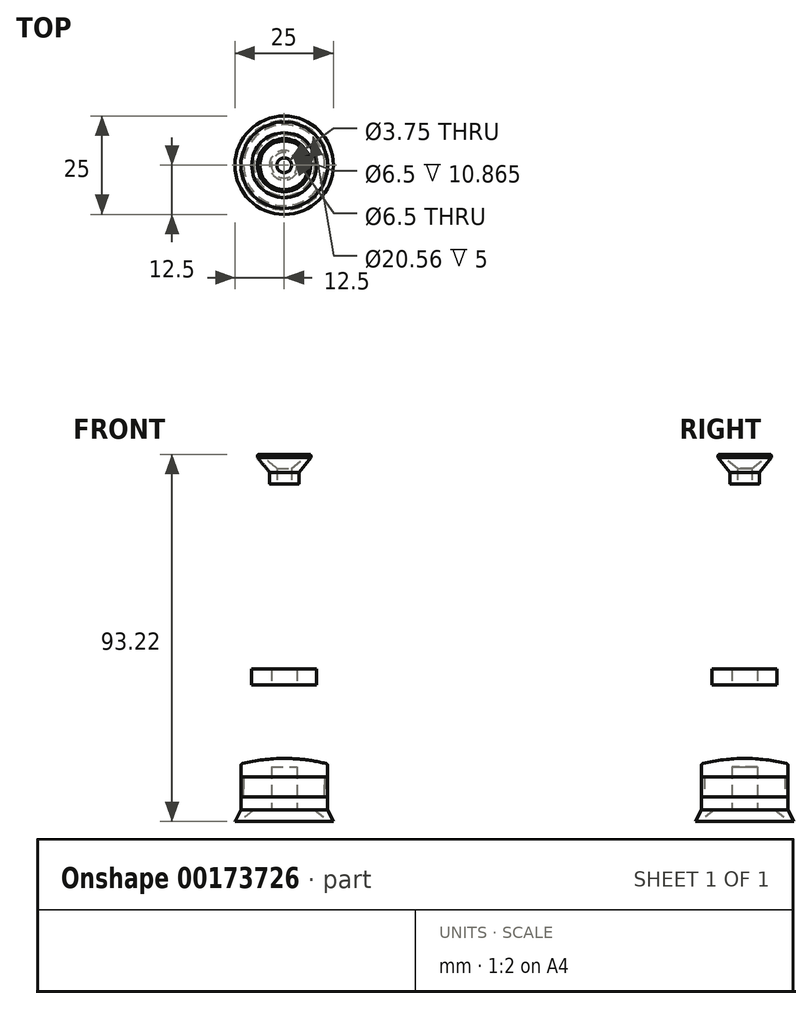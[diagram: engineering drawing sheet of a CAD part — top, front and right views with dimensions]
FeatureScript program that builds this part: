
annotation { "Feature Type Name" : "Feature", "Feature Type Description" : "" }
export const myFeature = defineFeature(function(context is Context, id is Id, definition is map)
    precondition{}
    {
        {
            var Q0;
            Q0=qCreatedBy(makeId("Front.planeOp"),FACE);
            var sketch = newSketch(context, id + "F0", { "sketchPlane" : qUnion([Q0])});
            skLineSegment(sketch, "E0.bottom", {"start": v(0, 0) * mm, "end": v(9, 0) * mm});
            skLineSegment(sketch, "E0.top", {"start": v(0, 18) * mm, "end": v(9, 18) * mm});
            skLineSegment(sketch, "E0.left", {"start": v(0, 0) * mm, "end": v(0, 18) * mm});
            skLineSegment(sketch, "E0.right", {"start": v(9, 0) * mm, "end": v(9, 18) * mm});
            skArc(sketch, "E1", {"start": v(9, 14.86) * mm, "mid": v(4.77, 17.2) * mm, "end": v(0, 18) * mm});
            skLineSegment(sketch, "E2.bottom", {"start": v(0, 0) * mm, "end": v(3.25, 0) * mm});
            skLineSegment(sketch, "E2.top", {"start": v(0, 15) * mm, "end": v(3.25, 15) * mm});
            skLineSegment(sketch, "E2.left", {"start": v(0, 0) * mm, "end": v(0, 15) * mm});
            skLineSegment(sketch, "E2.right", {"start": v(3.25, 0) * mm, "end": v(3.25, 15) * mm});
            skLineSegment(sketch, "E3.bottom", {"start": v(3.25, 0) * mm, "end": v(8.25, 0) * mm});
            skLineSegment(sketch, "E3.top", {"start": v(3.25, 4) * mm, "end": v(8.25, 4) * mm});
            skLineSegment(sketch, "E3.left", {"start": v(3.25, 0) * mm, "end": v(3.25, 4) * mm});
            skLineSegment(sketch, "E3.right", {"start": v(8.25, 0) * mm, "end": v(8.25, 4) * mm});
            skSolve(sketch);
        }
        {
            var Q0;
            {var subQ2=sQuery(id+"F0.wireOp",EDGE,"E0.bottom");Q0=makeQuery(id+"F0.imprint","IMPRINT",FACE,{"disambiguationData":[TD([[makeQuery(id+"F0.imprint","IMPRINT",EDGE,{"derivedFrom":subQ2}),1.0]])]});}
            var Q1;
            Q1=sQuery(id+"F0.wireOp",EDGE,"E0.left");
            revolve(context, id + "F1", {"entities" : qUnion([Q0]), "axis" : qUnion([Q1]), "revolveType" : RevolveType.FULL});
        }
        {
            var Q0;
            Q0=qCreatedBy(makeId("Front.planeOp"),FACE);
            var sketch = newSketch(context, id + "F2", { "sketchPlane" : qUnion([Q0])});
            skLineSegment(sketch, "E4.bottom", {"start": v(0, 50) * mm, "end": v(6.75, 50) * mm});
            skLineSegment(sketch, "E4.top", {"start": v(0, 58.5) * mm, "end": v(6.75, 58.5) * mm});
            skLineSegment(sketch, "E4.left", {"start": v(0, 50) * mm, "end": v(0, 58.5) * mm});
            skLineSegment(sketch, "E4.right", {"start": v(6.75, 50) * mm, "end": v(6.75, 58.5) * mm});
            skLineSegment(sketch, "E5.bottom", {"start": v(0, 50) * mm, "end": v(5.5, 50) * mm});
            skLineSegment(sketch, "E5.top", {"start": v(0, 51) * mm, "end": v(5.5, 51) * mm});
            skLineSegment(sketch, "E5.left", {"start": v(0, 50) * mm, "end": v(0, 51) * mm});
            skLineSegment(sketch, "E5.right", {"start": v(5.5, 50) * mm, "end": v(5.5, 51) * mm});
            skLineSegment(sketch, "E6.bottom", {"start": v(0, 51) * mm, "end": v(3.75, 51) * mm});
            skLineSegment(sketch, "E6.top", {"start": v(0, 54) * mm, "end": v(3.75, 54) * mm});
            skLineSegment(sketch, "E6.left", {"start": v(0, 51) * mm, "end": v(0, 54) * mm});
            skLineSegment(sketch, "E6.right", {"start": v(3.75, 51) * mm, "end": v(3.75, 54) * mm});
            skLineSegment(sketch, "E7", {"start": v(3.75, 54) * mm, "end": v(6.75, 57.75) * mm});
            skPoint(sketch, "E8.oppositeSnap0", {"position": v(1.87, 54) * mm});
            skLineSegment(sketch, "E8.bottom", {"start": v(0, 50) * mm, "end": v(1.87, 50) * mm});
            skLineSegment(sketch, "E8.top", {"start": v(0, 58.5) * mm, "end": v(1.87, 58.5) * mm});
            skLineSegment(sketch, "E8.right", {"start": v(1.87, 50) * mm, "end": v(1.87, 58.5) * mm});
            skLineSegment(sketch, "E9", {"start": v(1.87, 55) * mm, "end": v(6.2, 58.5) * mm});
            skArc(sketch, "E10", {"start": v(6.75, 58.05) * mm, "mid": v(6.73, 58.3) * mm, "end": v(6.6, 58.5) * mm});
            skSolve(sketch);
        }
        {
            var Q0;
            {var subQ0=sQuery(id+"F2.wireOp",EDGE,"E7");Q0=makeQuery(id+"F2.imprint","IMPRINT",FACE,{"disambiguationData":[TD([[makeQuery(id+"F2.imprint","IMPRINT",EDGE,{"derivedFrom":subQ0}),1.0]])]});}
            var Q1;
            {var subQ0=sQuery(id+"F2.wireOp",EDGE,"E6.right");Q1=makeQuery(id+"F2.imprint","IMPRINT",FACE,{"disambiguationData":[TD([[makeQuery(id+"F2.imprint","IMPRINT",EDGE,{"derivedFrom":subQ0}),1.0]])]});}
            var Q2;
            {var subQ4=sQuery(id+"F2.wireOp",EDGE,"E5.bottom");Q2=makeQuery(id+"F2.imprint","IMPRINT",FACE,{"disambiguationData":[TD([[makeQuery(id+"F2.imprint","IMPRINT",EDGE,{"derivedFrom":subQ4}),1.0]])]});}
            var Q3;
            Q3=sQuery(id+"F2.wireOp",EDGE,"E4.left");
            revolve(context, id + "F3", {"entities" : qUnion([Q0, Q1, Q2]), "axis" : qUnion([Q3]), "revolveType" : RevolveType.FULL});
        }
        {
            var Q0;
            Q0=makeQuery(id+"F3.opRevolve","SWEPT_EDGE",EDGE,{"disambiguationData":[OSD([sQuery(id+"F2.wireOp",EDGE,"E5.top"),sQuery(id+"F2.wireOp",EDGE,"E5.right")])]});
            fillet(context, id + "F4", {"entities" : qUnion([Q0]), "radius" : .2 * mm, "tangentPropagation" : true, "allowEdgeOverflow" : false});
        }
        {
            var Q0;
            Q0=qCreatedBy(makeId("Front.planeOp"),FACE);
            var sketch = newSketch(context, id + "F5", { "sketchPlane" : qUnion([Q0])});
            skLineSegment(sketch, "E11.bottom", {"start": v(0, -34.72) * mm, "end": v(12.5, -34.72) * mm});
            skLineSegment(sketch, "E11.top", {"start": v(0, -18.72) * mm, "end": v(12.5, -18.72) * mm});
            skLineSegment(sketch, "E11.left", {"start": v(0, -34.72) * mm, "end": v(0, -18.72) * mm});
            skLineSegment(sketch, "E11.right", {"start": v(12.5, -34.72) * mm, "end": v(12.5, -18.72) * mm});
            skLineSegment(sketch, "E12", {"start": v(12.5, -31.72) * mm, "end": v(0, -31.72) * mm});
            skLineSegment(sketch, "E13", {"start": v(11, -31.72) * mm, "end": v(11, -18.72) * mm});
            skLineSegment(sketch, "E14", {"start": v(11, -31.72) * mm, "end": v(12.5, -34.72) * mm});
            skLineSegment(sketch, "E15", {"start": v(11.37, -34.72) * mm, "end": v(7.7, -31.72) * mm});
            skLineSegment(sketch, "E16.bottom", {"start": v(3.25, -31.72) * mm, "end": v(0, -31.72) * mm});
            skLineSegment(sketch, "E16.top", {"start": v(3.25, -20.86) * mm, "end": v(0, -20.86) * mm});
            skLineSegment(sketch, "E16.left", {"start": v(3.25, -31.72) * mm, "end": v(3.25, -20.86) * mm});
            skLineSegment(sketch, "E16.right", {"start": v(0, -31.72) * mm, "end": v(0, -20.86) * mm});
            skArc(sketch, "E17", {"start": v(12.5, -20.51) * mm, "mid": v(6.31, -19.17) * mm, "end": v(0, -18.72) * mm});
            skLineSegment(sketch, "E18.left", {"start": v(12.5, -23.07) * mm, "end": v(12.5, -28.07) * mm});
            skLineSegment(sketch, "E19.bottom", {"start": v(11, -23.44) * mm, "end": v(10.28, -23.44) * mm});
            skLineSegment(sketch, "E19.top", {"start": v(11, -28.44) * mm, "end": v(10.28, -28.44) * mm});
            skLineSegment(sketch, "E19.left", {"start": v(11, -23.44) * mm, "end": v(11, -28.44) * mm});
            skLineSegment(sketch, "E19.right", {"start": v(10.28, -23.44) * mm, "end": v(10.28, -28.44) * mm});
            skSolve(sketch);
        }
        {
            var Q0;
            {var subQ11=sQuery(id+"F5.wireOp",EDGE,"E16.top");Q0=makeQuery(id+"F5.imprint","IMPRINT",FACE,{"disambiguationData":[TD([[makeQuery(id+"F5.imprint","IMPRINT",EDGE,{"derivedFrom":subQ11}),-1.0]])]});}
            var Q1;
            {var subQ0=sQuery(id+"F5.wireOp",EDGE,"E14");Q1=makeQuery(id+"F5.imprint","IMPRINT",FACE,{"disambiguationData":[TD([[makeQuery(id+"F5.imprint","IMPRINT",EDGE,{"derivedFrom":subQ0}),-1.0]])]});}
            var Q2;
            Q2=sQuery(id+"F5.wireOp",EDGE,"E16.right");
            revolve(context, id + "F6", {"entities" : qUnion([Q0, Q1]), "axis" : qUnion([Q2]), "revolveType" : RevolveType.FULL});
        }
        {
            var Q0;
            Q0=makeQuery(id+"F5.imprint","IMPRINT",FACE,{"disambiguationData":[TD([[makeQuery(id+"F5.imprint","IMPRINT",EDGE,{"derivedFrom":sQuery(id+"F5.wireOp",EDGE,"E19.bottom")}),1.0]])]});
            var Q1;
            Q1=makeQuery(id+"F6.opRevolve","SWEPT_FACE",FACE,{"disambiguationData":[OSD([sQuery(id+"F5.wireOp",EDGE,"E19.right")])]});
            revolve(context, id + "F7", {"entities" : qUnion([Q0]), "axis" : qUnion([Q1]), "revolveType" : RevolveType.FULL});
        }
        {
            var Q0;
            Q0=makeQuery(id+"F6.opRevolve","SWEPT_EDGE",EDGE,{"disambiguationData":[OSD([sQuery(id+"F5.wireOp",EDGE,"E13"),sQuery(id+"F5.wireOp",EDGE,"E17")])]});
            fillet(context, id + "F8", {"entities" : qUnion([Q0]), "radius" : .5 * mm, "tangentPropagation" : true, "allowEdgeOverflow" : false});
        }
    });
